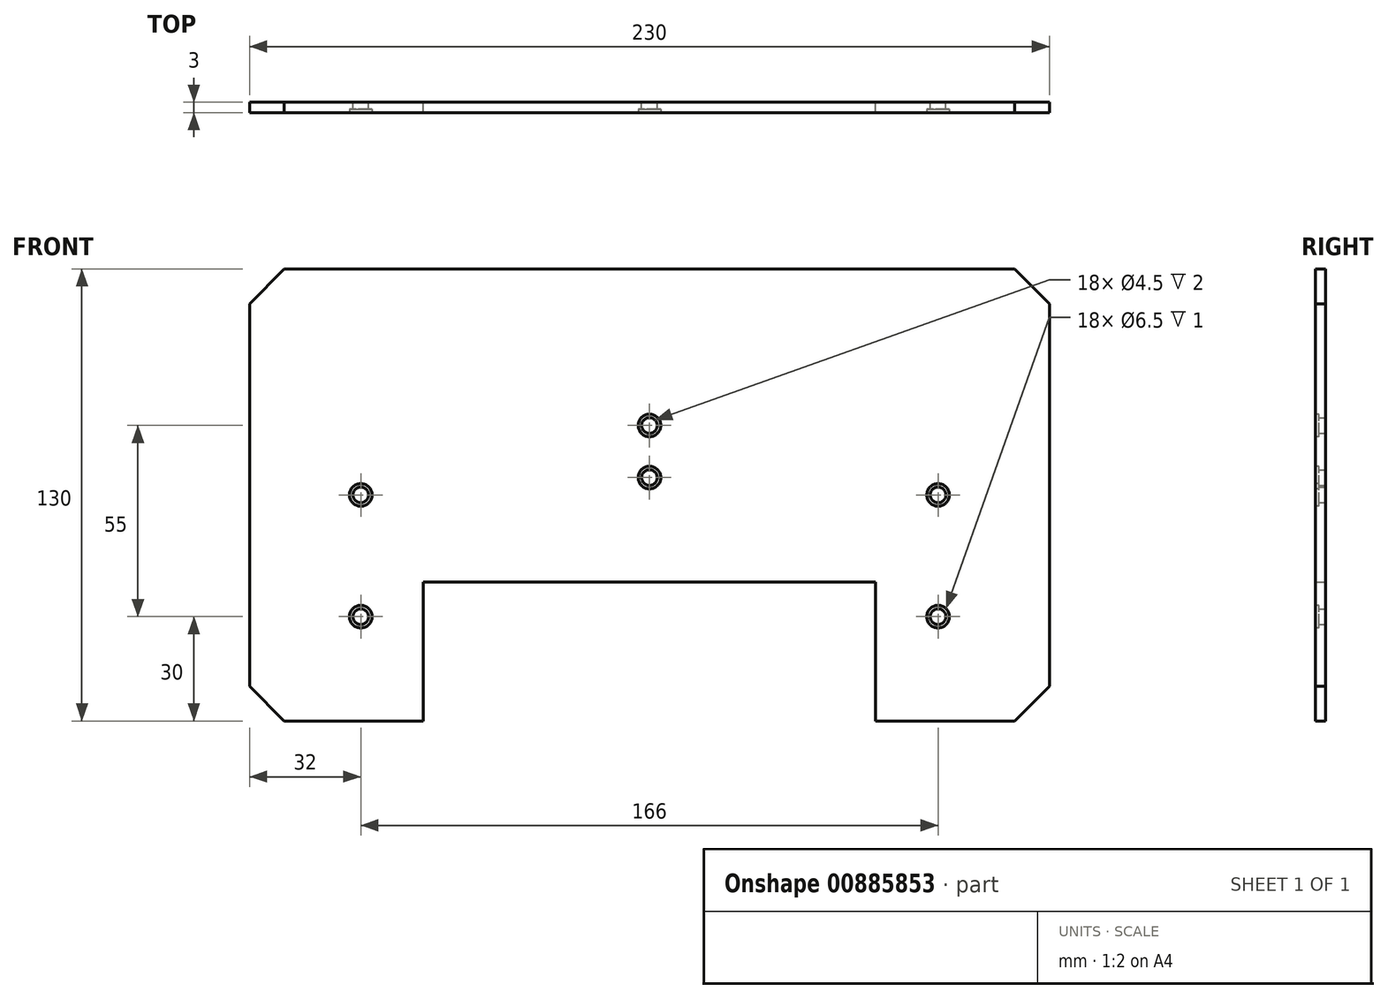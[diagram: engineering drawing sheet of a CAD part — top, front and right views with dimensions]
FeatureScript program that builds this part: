
annotation { "Feature Type Name" : "Feature", "Feature Type Description" : "" }
export const myFeature = defineFeature(function(context is Context, id is Id, definition is map)
    precondition{}
    {
        {
            var Q0;
            Q0=qCreatedBy(makeId("Front.planeOp"),FACE);
            var sketch = newSketch(context, id + "F0", { "sketchPlane" : qUnion([Q0])});
            skLineSegment(sketch, "E0.bottom", {"start": v(-115, 65) * mm, "end": v(115, 65) * mm});
            skLineSegment(sketch, "E0.top", {"start": v(-115, -65) * mm, "end": v(-65, -65) * mm});
            skLineSegment(sketch, "E0.left", {"start": v(-115, 65) * mm, "end": v(-115, -65) * mm});
            skLineSegment(sketch, "E0.right", {"start": v(115, 65) * mm, "end": v(115, -65) * mm});
            skPoint(sketch, "E0.middle", {"position": v(0, 0) * mm});
            skLineSegment(sketch, "E1", {"start": v(0, -25) * mm, "end": v(-65, -25) * mm});
            skLineSegment(sketch, "E2", {"start": v(-65, -25) * mm, "end": v(-65, -65) * mm});
            skLineSegment(sketch, "E3.MirrorCS", {"start": v(0, -25) * mm, "end": v(65, -25) * mm});
            skLineSegment(sketch, "E4.MirrorCS", {"start": v(65, -25) * mm, "end": v(65, -65) * mm});
            skCircle(sketch, "E5", {"center": v(-83, -35) * mm, "radius": 2.25 * mm});
            skCircle(sketch, "E6", {"center": v(-83, 0) * mm, "radius": 2.25 * mm});
            skCircle(sketch, "E7", {"center": v(0, 5) * mm, "radius": 2.25 * mm});
            skCircle(sketch, "E8", {"center": v(0, 20) * mm, "radius": 2.25 * mm});
            skCircle(sketch, "E9.MirrorC", {"center": v(83, -35) * mm, "radius": 2.25 * mm});
            skCircle(sketch, "E10.MirrorC", {"center": v(83, 0) * mm, "radius": 2.25 * mm});
            skPoint(sketch, "E11.start.orphan", {"position": v(0, -65) * mm});
            skLineSegment(sketch, "E12.trimOffspring", {"start": v(65, -65) * mm, "end": v(115, -65) * mm});
            skSolve(sketch);
        }
        {
            var Q0;
            Q0 = qSketchRegion(id + "F0", true);
            extrude(context, id + "F1", {"entities" : qUnion([Q0]), "depth" : 3 * mm, "offsetDistance" : 25 * mm});
        }
        {
            var Q0;
            Q0=makeQuery(id+"F1.opExtrude","SWEPT_EDGE",EDGE,{"disambiguationData":[OSD([sQuery(id+"F0.wireOp",EDGE,"E0.bottom"),sQuery(id+"F0.wireOp",EDGE,"E0.left")])]});
            var Q1;
            Q1=makeQuery(id+"F1.opExtrude","SWEPT_EDGE",EDGE,{"disambiguationData":[OSD([sQuery(id+"F0.wireOp",EDGE,"E0.bottom"),sQuery(id+"F0.wireOp",EDGE,"E0.right")])]});
            var Q2;
            Q2=makeQuery(id+"F1.opExtrude","SWEPT_EDGE",EDGE,{"disambiguationData":[OSD([sQuery(id+"F0.wireOp",EDGE,"E0.right"),sQuery(id+"F0.wireOp",EDGE,"E12.trimOffspring")])]});
            var Q3;
            Q3=makeQuery(id+"F1.opExtrude","SWEPT_EDGE",EDGE,{"disambiguationData":[OSD([sQuery(id+"F0.wireOp",EDGE,"E0.top"),sQuery(id+"F0.wireOp",EDGE,"E0.left")])]});
            chamfer(context, id + "F2", {"entities" : qUnion([Q0, Q1, Q2, Q3]), "width" : 10 * mm, "tangentPropagation" : true});
        }
        {
            var Q0;
            Q0=makeQuery(id+"F1.opExtrude","CAP_FACE",FACE,{"disambiguationData":[OSD([sQuery(id+"F0.wireOp",EDGE,"E0.bottom"),sQuery(id+"F0.wireOp",EDGE,"E0.top"),sQuery(id+"F0.wireOp",EDGE,"E0.left"),sQuery(id+"F0.wireOp",EDGE,"E0.right"),sQuery(id+"F0.wireOp",EDGE,"E1"),sQuery(id+"F0.wireOp",EDGE,"E2"),sQuery(id+"F0.wireOp",EDGE,"E3.MirrorCS"),sQuery(id+"F0.wireOp",EDGE,"E4.MirrorCS"),sQuery(id+"F0.wireOp",EDGE,"E5"),sQuery(id+"F0.wireOp",EDGE,"E6"),sQuery(id+"F0.wireOp",EDGE,"E7"),sQuery(id+"F0.wireOp",EDGE,"E8"),sQuery(id+"F0.wireOp",EDGE,"E9.MirrorC"),sQuery(id+"F0.wireOp",EDGE,"E10.MirrorC"),sQuery(id+"F0.wireOp",EDGE,"E12.trimOffspring")])],"isStart":false});
            var sketch = newSketch(context, id + "F3", { "sketchPlane" : qUnion([Q0])});
            skCircle(sketch, "E13", {"center": v(-83, 0) * mm, "radius": 3.25 * mm});
            skCircle(sketch, "E14", {"center": v(-83, -35) * mm, "radius": 3.25 * mm});
            skCircle(sketch, "E15", {"center": v(0, 20) * mm, "radius": 3.25 * mm});
            skCircle(sketch, "E16", {"center": v(0, 5) * mm, "radius": 3.25 * mm});
            skCircle(sketch, "E17", {"center": v(83, 0) * mm, "radius": 3.25 * mm});
            skCircle(sketch, "E18", {"center": v(83, -35) * mm, "radius": 3.25 * mm});
            skSolve(sketch);
        }
        {
            var Q0;
            Q0 = qSketchRegion(id + "F3", true);
            extrude(context, id + "F4", {"entities" : qUnion([Q0]), "operationType" : NewBodyOperationType.REMOVE, "oppositeDirection" : true, "depth" : 1 * mm, "offsetDistance" : 25 * mm});
        }
    });
